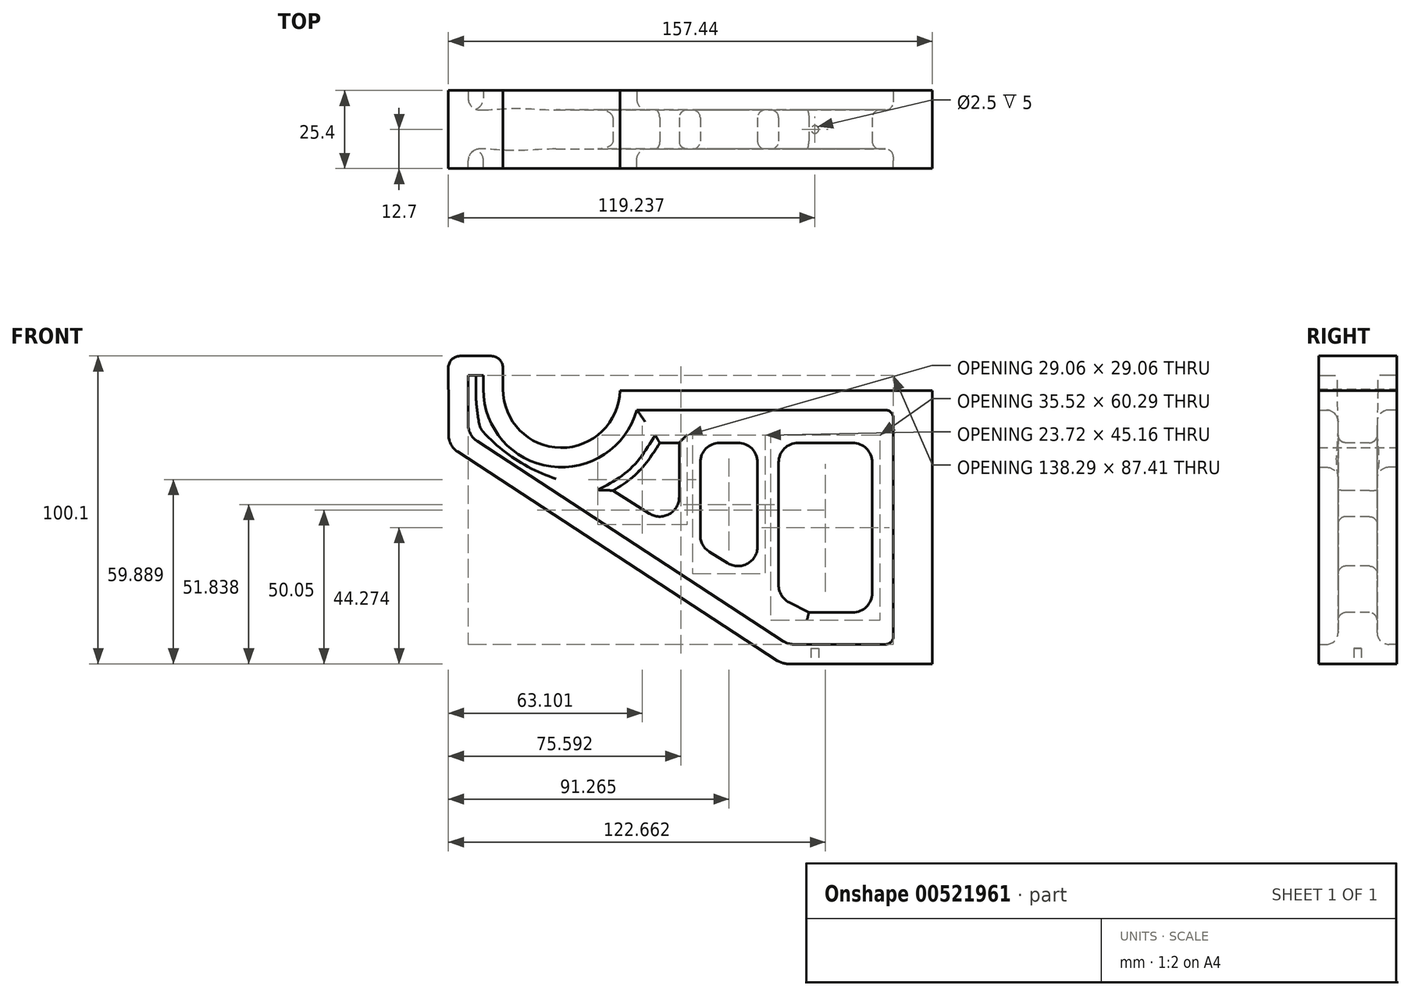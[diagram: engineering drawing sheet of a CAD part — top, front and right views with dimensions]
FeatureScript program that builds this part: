
annotation { "Feature Type Name" : "Feature", "Feature Type Description" : "" }
export const myFeature = defineFeature(function(context is Context, id is Id, definition is map)
    precondition{}
    {
        {
            var Q0;
            Q0=qCreatedBy(makeId("Front.planeOp"),FACE);
            var sketch = newSketch(context, id + "F0", { "sketchPlane" : qUnion([Q0])});
            skLineSegment(sketch, "E0.0", {"start": v(-84.04, 39.62) * mm, "end": v(-84.04, 21.17) * mm});
            skLineSegment(sketch, "E0.1", {"start": v(66.96, 39.19) * mm, "end": v(-28.3, 39.19) * mm});
            skLineSegment(sketch, "E0.2", {"start": v(-84.04, 21.17) * mm, "end": v(24.5, -49.71) * mm});
            skLineSegment(sketch, "E0.3", {"start": v(24.5, -49.71) * mm, "end": v(66.96, -49.71) * mm});
            skLineSegment(sketch, "E0.4", {"start": v(66.96, -49.71) * mm, "end": v(66.96, 39.19) * mm});
            skArc(sketch, "E1", {"start": v(-66.4, 39.62) * mm, "mid": v(-47.56, 20.57) * mm, "end": v(-28.3, 39.19) * mm});
            skLineSegment(sketch, "E2.bottom", {"start": v(-84.04, 39.62) * mm, "end": v(-84.13, 39.62) * mm});
            skLineSegment(sketch, "E2.top", {"start": v(-66.4, 50.4) * mm, "end": v(-84.13, 50.4) * mm});
            skLineSegment(sketch, "E2.left", {"start": v(-66.4, 39.62) * mm, "end": v(-66.4, 50.4) * mm});
            skLineSegment(sketch, "E2.right", {"start": v(-84.13, 39.62) * mm, "end": v(-84.13, 50.4) * mm});
            skLineSegment(sketch, "E3", {"start": v(-47.34, 83.6) * mm, "end": v(-47.34, -33.91) * mm, "construction": true});
            skLineSegment(sketch, "E4", {"start": v(-97.5, 39.62) * mm, "end": v(58.93, 39.62) * mm, "construction": true});
            skLineSegment(sketch, "E5", {"start": v(66.96, -49.71) * mm, "end": v(66.96, 87.18) * mm, "construction": true});
            skSolve(sketch);
        }
        {
            var Q0;
            Q0=makeQuery(id+"F0.imprint","IMPRINT",FACE,{"disambiguationData":[TD([[makeQuery(id+"F0.imprint","IMPRINT",EDGE,{"derivedFrom":sQuery(id+"F0.wireOp",EDGE,"E0.0")}),1.0]])]});
            extrude(context, id + "F1", {"entities" : qUnion([Q0]), "depth" : 6.35 * mm, "offsetDistance" : 25.4 * mm, "hasSecondDirection" : true, "secondDirectionOppositeDirection" : true, "secondDirectionDepth" : 6.35 * mm});
        }
        {
            var Q0;
            Q0=makeQuery(id+"F1.opExtrude","CAP_FACE",FACE,{"disambiguationData":[OSD([sQuery(id+"F0.wireOp",EDGE,"E0.0"),sQuery(id+"F0.wireOp",EDGE,"E0.1"),sQuery(id+"F0.wireOp",EDGE,"E0.2"),sQuery(id+"F0.wireOp",EDGE,"E0.3"),sQuery(id+"F0.wireOp",EDGE,"E0.4"),sQuery(id+"F0.wireOp",EDGE,"E1"),sQuery(id+"F0.wireOp",EDGE,"caf5afc5-a840-4588-9689-efeb098a28d0.trimOffspring")])],"isStart":false});
            shell(context, id + "F2", {"entities" : qUnion([Q0]), "thickness" : 6.35 * mm});
        }
        {
            var Q0;
            Q0=makeQuery(id+"F1.opExtrude","SWEPT_EDGE",EDGE,{"disambiguationData":[OSD([sQuery(id+"F0.wireOp",EDGE,"E0.0"),sQuery(id+"F0.wireOp",EDGE,"E0.2")])]});
            var Q1;
            Q1=makeQuery(id+"F2.opShell","OFFSET_EDGE",EDGE,{"disambiguationData":[OSD([sQuery(id+"F0.wireOp",EDGE,"E0.0"),sQuery(id+"F0.wireOp",EDGE,"E0.2")])]});
            var Q2;
            Q2=makeQuery(id+"F2.opShell","OFFSET_EDGE",EDGE,{"disambiguationData":[OSD([sQuery(id+"F0.wireOp",EDGE,"E0.2"),sQuery(id+"F0.wireOp",EDGE,"E0.3")])]});
            var Q3;
            Q3=makeQuery(id+"F1.opExtrude","SWEPT_EDGE",EDGE,{"disambiguationData":[OSD([sQuery(id+"F0.wireOp",EDGE,"E0.2"),sQuery(id+"F0.wireOp",EDGE,"E0.3")])]});
            var Q4;
            Q4=makeQuery(id+"F1.opExtrude","SWEPT_EDGE",EDGE,{"disambiguationData":[OSD([sQuery(id+"F0.wireOp",EDGE,"E0.0"),sQuery(id+"F0.wireOp",EDGE,"caf5afc5-a840-4588-9689-efeb098a28d0.trimOffspring")])]});
            fillet(context, id + "F3", {"entities" : qUnion([Q0, Q1, Q2, Q3, Q4]), "radius" : 6.35 * mm, "tangentPropagation" : true, "allowEdgeOverflow" : false});
        }
        {
            var Q0;
            Q0=makeQuery(id+"F1.opExtrude","SWEPT_BODY",BODY,{"disambiguationData":[OSD([sQuery(id+"F0.wireOp",EDGE,"E0.0"),sQuery(id+"F0.wireOp",EDGE,"E0.1"),sQuery(id+"F0.wireOp",EDGE,"E0.2"),sQuery(id+"F0.wireOp",EDGE,"E0.3"),sQuery(id+"F0.wireOp",EDGE,"E0.4"),sQuery(id+"F0.wireOp",EDGE,"E1"),sQuery(id+"F0.wireOp",EDGE,"caf5afc5-a840-4588-9689-efeb098a28d0.trimOffspring")])]});
            var Q1;
            Q1=makeQuery(id+"F1.opExtrude","CAP_FACE",FACE,{"disambiguationData":[OSD([sQuery(id+"F0.wireOp",EDGE,"E0.0"),sQuery(id+"F0.wireOp",EDGE,"E0.1"),sQuery(id+"F0.wireOp",EDGE,"E0.2"),sQuery(id+"F0.wireOp",EDGE,"E0.3"),sQuery(id+"F0.wireOp",EDGE,"E0.4"),sQuery(id+"F0.wireOp",EDGE,"E1"),sQuery(id+"F0.wireOp",EDGE,"caf5afc5-a840-4588-9689-efeb098a28d0.trimOffspring")])],"isStart":true});
            mirror(context, id + "F4", {"operationType" : NewBodyOperationType.ADD, "entities" : qUnion([Q0]), "mirrorPlane" : qUnion([Q1])});
        }
        {
            var Q0;
            {var subQ0=makeQuery(id+"F1.opExtrude","SWEPT_EDGE",EDGE,{"disambiguationData":[OSD([sQuery(id+"F0.wireOp",EDGE,"E2.top"),sQuery(id+"F0.wireOp",EDGE,"E2.right")])]});Q0=makeQuery(id+"F4.boolean.opBoolean","MERGE",EDGE,{"derivedFrom":[subQ0,makeQuery(id+"F4.opPattern","COPY",EDGE,{"derivedFrom":subQ0,"instanceName":"1"})]});}
            var Q1;
            {var subQ0=makeQuery(id+"F1.opExtrude","SWEPT_EDGE",EDGE,{"disambiguationData":[OSD([sQuery(id+"F0.wireOp",EDGE,"E2.top"),sQuery(id+"F0.wireOp",EDGE,"E2.left")])]});Q1=makeQuery(id+"F4.boolean.opBoolean","MERGE",EDGE,{"derivedFrom":[subQ0,makeQuery(id+"F4.opPattern","COPY",EDGE,{"derivedFrom":subQ0,"instanceName":"1"})]});}
            var Q2;
            {var subQ0=sQuery(id+"F0.wireOp",EDGE,"E0.2");Q2=makeQuery(id+"F2.opShell","OFFSET_EDGE",EDGE,{"disambiguationData":[OSD([subQ0]),TDD([makeQuery(id+"F1.opExtrude","CAP_EDGE",EDGE,{"disambiguationData":[OSD([subQ0])],"isStart":true})])]});}
            var Q3;
            {var subQ0=sQuery(id+"F0.wireOp",EDGE,"E0.1");Q3=makeQuery(id+"F2.opShell","OFFSET_EDGE",EDGE,{"disambiguationData":[OSD([subQ0]),TDD([makeQuery(id+"F1.opExtrude","CAP_EDGE",EDGE,{"disambiguationData":[OSD([subQ0])],"isStart":true})])]});}
            var Q4;
            {var subQ0=sQuery(id+"F0.wireOp",EDGE,"E1");Q4=makeQuery(id+"F2.opShell","OFFSET_EDGE",EDGE,{"disambiguationData":[OSD([subQ0]),TDD([makeQuery(id+"F1.opExtrude","CAP_EDGE",EDGE,{"disambiguationData":[OSD([subQ0])],"isStart":true})])]});}
            var Q5;
            {var subQ0=sQuery(id+"F0.wireOp",EDGE,"E0.1");Q5=makeQuery(id+"F4.opPattern","COPY",EDGE,{"derivedFrom":makeQuery(id+"F2.opShell","OFFSET_EDGE",EDGE,{"disambiguationData":[OSD([subQ0]),TDD([makeQuery(id+"F1.opExtrude","CAP_EDGE",EDGE,{"disambiguationData":[OSD([subQ0])],"isStart":true})])]}),"instanceName":"1"});}
            var Q6;
            {var subQ0=sQuery(id+"F0.wireOp",EDGE,"E0.2");Q6=makeQuery(id+"F4.opPattern","COPY",EDGE,{"derivedFrom":makeQuery(id+"F2.opShell","OFFSET_EDGE",EDGE,{"disambiguationData":[OSD([subQ0]),TDD([makeQuery(id+"F1.opExtrude","CAP_EDGE",EDGE,{"disambiguationData":[OSD([subQ0])],"isStart":true})])]}),"instanceName":"1"});}
            var Q7;
            {var subQ0=sQuery(id+"F0.wireOp",EDGE,"E1");Q7=makeQuery(id+"F4.opPattern","COPY",EDGE,{"derivedFrom":makeQuery(id+"F2.opShell","OFFSET_EDGE",EDGE,{"disambiguationData":[OSD([subQ0]),TDD([makeQuery(id+"F1.opExtrude","CAP_EDGE",EDGE,{"disambiguationData":[OSD([subQ0])],"isStart":true})])]}),"instanceName":"1"});}
            fillet(context, id + "F5", {"entities" : qUnion([Q0, Q1, Q2, Q3, Q4, Q5, Q6, Q7]), "radius" : 3.8 * mm, "tangentPropagation" : true, "allowEdgeOverflow" : false});
        }
        {
            var Q0;
            Q0=makeQuery(id+"F2.opShell","OFFSET_FACE",FACE,{"disambiguationData":[OSD([sQuery(id+"F0.wireOp",EDGE,"E0.0"),sQuery(id+"F0.wireOp",EDGE,"E0.1"),sQuery(id+"F0.wireOp",EDGE,"E0.2"),sQuery(id+"F0.wireOp",EDGE,"E0.3"),sQuery(id+"F0.wireOp",EDGE,"E0.4"),sQuery(id+"F0.wireOp",EDGE,"E1"),sQuery(id+"F0.wireOp",EDGE,"E2.bottom"),sQuery(id+"F0.wireOp",EDGE,"E2.top"),sQuery(id+"F0.wireOp",EDGE,"E2.left"),sQuery(id+"F0.wireOp",EDGE,"E2.right")])]});
            cPlane(context, id + "F6", {"entities" : qUnion([Q0]), "cplaneType" : CPlaneType.OFFSET, "offset" : 0 * mm, "width" : 152.4 * mm, "height" : 152.4 * mm});
        }
        {
            var Q0;
            Q0=qCreatedBy(id+"F6.planeOp",FACE);
            var sketch = newSketch(context, id + "F7", { "sketchPlane" : qUnion([Q0])});
            skLineSegment(sketch, "E6", {"start": v(29.66, 22.17) * mm, "end": v(47.4, 22.17) * mm});
            skLineSegment(sketch, "E7", {"start": v(53.75, 15.82) * mm, "end": v(53.75, -26.7) * mm});
            skLineSegment(sketch, "E8", {"start": v(47.4, -33.04) * mm, "end": v(33.14, -33.04) * mm});
            skLineSegment(sketch, "E9", {"start": v(33.14, -33.04) * mm, "end": v(26.75, -29.74) * mm});
            skLineSegment(sketch, "E10", {"start": v(23.31, -24.1) * mm, "end": v(23.31, 15.82) * mm});
            skLineSegment(sketch, "E11", {"start": v(10.1, 22.17) * mm, "end": v(4.17, 22.17) * mm});
            skLineSegment(sketch, "E12", {"start": v(-2.18, 15.82) * mm, "end": v(-2.18, -7.91) * mm});
            skLineSegment(sketch, "E13", {"start": v(0.84, -13.32) * mm, "end": v(6.78, -16.97) * mm});
            skLineSegment(sketch, "E14", {"start": v(16.45, -11.56) * mm, "end": v(16.45, 15.82) * mm});
            skLineSegment(sketch, "E15", {"start": v(-15.4, 22.17) * mm, "end": v(-9.04, 22.17) * mm});
            skLineSegment(sketch, "E16", {"start": v(-9.04, 22.17) * mm, "end": v(-9.04, 4.53) * mm});
            skLineSegment(sketch, "E17", {"start": v(-18.8, -0.82) * mm, "end": v(-30.55, 6.66) * mm});
            skFitSpline(sketch, "E18", {"points": [v(-30.55, 6.66) * mm, v(-15.4, 22.17) * mm], "startDerivative": vector(20.62, 11.16) * mm, "endDerivative": vector(13.57, 22.58) * mm});
            skPoint(sketch, "E19.visualSharp", {"position": v(53.75, 22.17) * mm});
            skArc(sketch, "E19.filletArc", {"start": v(53.75, 15.82) * mm, "mid": v(51.9, 20.3) * mm, "end": v(47.4, 22.17) * mm});
            skPoint(sketch, "E20.visualSharp", {"position": v(23.31, 22.17) * mm});
            skArc(sketch, "E20.filletArc", {"start": v(29.66, 22.17) * mm, "mid": v(25.17, 20.3) * mm, "end": v(23.31, 15.82) * mm});
            skPoint(sketch, "E21.visualSharp", {"position": v(53.75, -33.04) * mm});
            skArc(sketch, "E21.filletArc", {"start": v(47.4, -33.04) * mm, "mid": v(51.9, -31.18) * mm, "end": v(53.75, -26.7) * mm});
            skPoint(sketch, "E22.visualSharp", {"position": v(16.45, 22.17) * mm});
            skArc(sketch, "E22.filletArc", {"start": v(16.45, 15.82) * mm, "mid": v(14.6, 20.3) * mm, "end": v(10.1, 22.17) * mm});
            skPoint(sketch, "E23.visualSharp", {"position": v(-2.18, 22.17) * mm});
            skArc(sketch, "E23.filletArc", {"start": v(4.17, 22.17) * mm, "mid": v(-0.32, 20.3) * mm, "end": v(-2.18, 15.82) * mm});
            skPoint(sketch, "E24.visualSharp", {"position": v(-9.04, -7.04) * mm});
            skArc(sketch, "E24.filletArc", {"start": v(-18.8, -0.82) * mm, "mid": v(-12.34, -1.03) * mm, "end": v(-9.04, 4.53) * mm});
            skPoint(sketch, "E25.visualSharp", {"position": v(16.45, -22.93) * mm});
            skArc(sketch, "E25.filletArc", {"start": v(6.78, -16.97) * mm, "mid": v(13.2, -17.1) * mm, "end": v(16.45, -11.56) * mm});
            skPoint(sketch, "E26.visualSharp", {"position": v(23.31, -27.96) * mm});
            skArc(sketch, "E26.filletArc", {"start": v(23.31, -24.1) * mm, "mid": v(24.24, -27.4) * mm, "end": v(26.75, -29.74) * mm});
            skPoint(sketch, "E27.visualSharp", {"position": v(-2.18, -11.46) * mm});
            skArc(sketch, "E27.filletArc", {"start": v(-2.18, -7.91) * mm, "mid": v(-1.38, -11) * mm, "end": v(0.84, -13.32) * mm});
            skSolve(sketch);
        }
        {
            var Q0;
            Q0=makeQuery(id+"F7.imprint","IMPRINT",FACE,{"disambiguationData":[TD([[makeQuery(id+"F7.imprint","IMPRINT",EDGE,{"derivedFrom":sQuery(id+"F7.wireOp",EDGE,"E15")}),-1.0]])]});
            var Q1;
            Q1=makeQuery(id+"F7.imprint","IMPRINT",FACE,{"disambiguationData":[TD([[makeQuery(id+"F7.imprint","IMPRINT",EDGE,{"derivedFrom":sQuery(id+"F7.wireOp",EDGE,"E11")}),1.0]])]});
            var Q2;
            Q2=makeQuery(id+"F7.imprint","IMPRINT",FACE,{"disambiguationData":[TD([[makeQuery(id+"F7.imprint","IMPRINT",EDGE,{"derivedFrom":sQuery(id+"F7.wireOp",EDGE,"E6")}),-1.0]])]});
            extrude(context, id + "F8", {"entities" : qUnion([Q0, Q1, Q2]), "operationType" : NewBodyOperationType.REMOVE, "oppositeDirection" : true, "depth" : 25.4 * mm, "offsetDistance" : 25.4 * mm, "hasSecondDirection" : true, "secondDirectionOppositeDirection" : false, "secondDirectionDepth" : 25.4 * mm});
        }
        {
            var Q0;
            Q0=makeQuery(id+"F8.boolean.opBoolean","INTERSECT",EDGE,{"derivedFrom":[makeQuery(id+"F4.opPattern","COPY",FACE,{"derivedFrom":makeQuery(id+"F2.opShell","OFFSET_FACE",FACE,{"disambiguationData":[OSD([sQuery(id+"F0.wireOp",EDGE,"E0.0"),sQuery(id+"F0.wireOp",EDGE,"E0.1"),sQuery(id+"F0.wireOp",EDGE,"E0.2"),sQuery(id+"F0.wireOp",EDGE,"E0.3"),sQuery(id+"F0.wireOp",EDGE,"E0.4"),sQuery(id+"F0.wireOp",EDGE,"E1"),sQuery(id+"F0.wireOp",EDGE,"E2.bottom"),sQuery(id+"F0.wireOp",EDGE,"E2.top"),sQuery(id+"F0.wireOp",EDGE,"E2.left"),sQuery(id+"F0.wireOp",EDGE,"E2.right")])]}),"instanceName":"1"}),makeQuery(id+"F8.opExtrude","SWEPT_FACE",FACE,{"disambiguationData":[OSD([sQuery(id+"F7.wireOp",EDGE,"E7")])]})]});
            var Q1;
            Q1=makeQuery(id+"F8.boolean.opBoolean","INTERSECT",EDGE,{"derivedFrom":[makeQuery(id+"F2.opShell","OFFSET_FACE",FACE,{"disambiguationData":[OSD([sQuery(id+"F0.wireOp",EDGE,"E0.0"),sQuery(id+"F0.wireOp",EDGE,"E0.1"),sQuery(id+"F0.wireOp",EDGE,"E0.2"),sQuery(id+"F0.wireOp",EDGE,"E0.3"),sQuery(id+"F0.wireOp",EDGE,"E0.4"),sQuery(id+"F0.wireOp",EDGE,"E1"),sQuery(id+"F0.wireOp",EDGE,"E2.bottom"),sQuery(id+"F0.wireOp",EDGE,"E2.top"),sQuery(id+"F0.wireOp",EDGE,"E2.left"),sQuery(id+"F0.wireOp",EDGE,"E2.right")])]}),makeQuery(id+"F8.opExtrude","SWEPT_FACE",FACE,{"disambiguationData":[OSD([sQuery(id+"F7.wireOp",EDGE,"E14")])]})]});
            var Q2;
            Q2=makeQuery(id+"F8.boolean.opBoolean","INTERSECT",EDGE,{"derivedFrom":[makeQuery(id+"F4.opPattern","COPY",FACE,{"derivedFrom":makeQuery(id+"F2.opShell","OFFSET_FACE",FACE,{"disambiguationData":[OSD([sQuery(id+"F0.wireOp",EDGE,"E0.0"),sQuery(id+"F0.wireOp",EDGE,"E0.1"),sQuery(id+"F0.wireOp",EDGE,"E0.2"),sQuery(id+"F0.wireOp",EDGE,"E0.3"),sQuery(id+"F0.wireOp",EDGE,"E0.4"),sQuery(id+"F0.wireOp",EDGE,"E1"),sQuery(id+"F0.wireOp",EDGE,"E2.bottom"),sQuery(id+"F0.wireOp",EDGE,"E2.top"),sQuery(id+"F0.wireOp",EDGE,"E2.left"),sQuery(id+"F0.wireOp",EDGE,"E2.right")])]}),"instanceName":"1"}),makeQuery(id+"F8.opExtrude","SWEPT_FACE",FACE,{"disambiguationData":[OSD([sQuery(id+"F7.wireOp",EDGE,"E16")])]})]});
            var Q3;
            Q3=makeQuery(id+"F4.opPattern","COPY",FACE,{"derivedFrom":makeQuery(id+"F2.opShell","OFFSET_FACE",FACE,{"disambiguationData":[OSD([sQuery(id+"F0.wireOp",EDGE,"E0.0"),sQuery(id+"F0.wireOp",EDGE,"E0.1"),sQuery(id+"F0.wireOp",EDGE,"E0.2"),sQuery(id+"F0.wireOp",EDGE,"E0.3"),sQuery(id+"F0.wireOp",EDGE,"E0.4"),sQuery(id+"F0.wireOp",EDGE,"E1"),sQuery(id+"F0.wireOp",EDGE,"E2.bottom"),sQuery(id+"F0.wireOp",EDGE,"E2.top"),sQuery(id+"F0.wireOp",EDGE,"E2.left"),sQuery(id+"F0.wireOp",EDGE,"E2.right")])]}),"instanceName":"1"});
            var Q4;
            Q4=makeQuery(id+"F8.boolean.opBoolean","INTERSECT",EDGE,{"derivedFrom":[makeQuery(id+"F2.opShell","OFFSET_FACE",FACE,{"disambiguationData":[OSD([sQuery(id+"F0.wireOp",EDGE,"E0.0"),sQuery(id+"F0.wireOp",EDGE,"E0.1"),sQuery(id+"F0.wireOp",EDGE,"E0.2"),sQuery(id+"F0.wireOp",EDGE,"E0.3"),sQuery(id+"F0.wireOp",EDGE,"E0.4"),sQuery(id+"F0.wireOp",EDGE,"E1"),sQuery(id+"F0.wireOp",EDGE,"E2.bottom"),sQuery(id+"F0.wireOp",EDGE,"E2.top"),sQuery(id+"F0.wireOp",EDGE,"E2.left"),sQuery(id+"F0.wireOp",EDGE,"E2.right")])]}),makeQuery(id+"F8.opExtrude","SWEPT_FACE",FACE,{"disambiguationData":[OSD([sQuery(id+"F7.wireOp",EDGE,"E10")])]})]});
            var Q5;
            Q5=makeQuery(id+"F8.boolean.opBoolean","INTERSECT",EDGE,{"derivedFrom":[makeQuery(id+"F2.opShell","OFFSET_FACE",FACE,{"disambiguationData":[OSD([sQuery(id+"F0.wireOp",EDGE,"E0.0"),sQuery(id+"F0.wireOp",EDGE,"E0.1"),sQuery(id+"F0.wireOp",EDGE,"E0.2"),sQuery(id+"F0.wireOp",EDGE,"E0.3"),sQuery(id+"F0.wireOp",EDGE,"E0.4"),sQuery(id+"F0.wireOp",EDGE,"E1"),sQuery(id+"F0.wireOp",EDGE,"E2.bottom"),sQuery(id+"F0.wireOp",EDGE,"E2.top"),sQuery(id+"F0.wireOp",EDGE,"E2.left"),sQuery(id+"F0.wireOp",EDGE,"E2.right")])]}),makeQuery(id+"F8.opExtrude","SWEPT_FACE",FACE,{"disambiguationData":[OSD([sQuery(id+"F7.wireOp",EDGE,"E16")])]})]});
            var Q6;
            Q6=makeQuery(id+"F8.boolean.opBoolean","INTERSECT",EDGE,{"derivedFrom":[makeQuery(id+"F2.opShell","OFFSET_FACE",FACE,{"disambiguationData":[OSD([sQuery(id+"F0.wireOp",EDGE,"E0.0"),sQuery(id+"F0.wireOp",EDGE,"E0.1"),sQuery(id+"F0.wireOp",EDGE,"E0.2"),sQuery(id+"F0.wireOp",EDGE,"E0.3"),sQuery(id+"F0.wireOp",EDGE,"E0.4"),sQuery(id+"F0.wireOp",EDGE,"E1"),sQuery(id+"F0.wireOp",EDGE,"E2.bottom"),sQuery(id+"F0.wireOp",EDGE,"E2.top"),sQuery(id+"F0.wireOp",EDGE,"E2.left"),sQuery(id+"F0.wireOp",EDGE,"E2.right")])]}),makeQuery(id+"F8.opExtrude","SWEPT_FACE",FACE,{"disambiguationData":[OSD([sQuery(id+"F7.wireOp",EDGE,"E18")])]})]});
            var Q7;
            Q7=makeQuery(id+"F8.boolean.opBoolean","INTERSECT",EDGE,{"derivedFrom":[makeQuery(id+"F2.opShell","OFFSET_FACE",FACE,{"disambiguationData":[OSD([sQuery(id+"F0.wireOp",EDGE,"E0.0"),sQuery(id+"F0.wireOp",EDGE,"E0.1"),sQuery(id+"F0.wireOp",EDGE,"E0.2"),sQuery(id+"F0.wireOp",EDGE,"E0.3"),sQuery(id+"F0.wireOp",EDGE,"E0.4"),sQuery(id+"F0.wireOp",EDGE,"E1"),sQuery(id+"F0.wireOp",EDGE,"E2.bottom"),sQuery(id+"F0.wireOp",EDGE,"E2.top"),sQuery(id+"F0.wireOp",EDGE,"E2.left"),sQuery(id+"F0.wireOp",EDGE,"E2.right")])]}),makeQuery(id+"F8.opExtrude","SWEPT_FACE",FACE,{"disambiguationData":[OSD([sQuery(id+"F7.wireOp",EDGE,"E15")])]})]});
            var Q8;
            {var subQ0=sQuery(id+"F0.wireOp",EDGE,"E0.4");Q8=makeQuery(id+"F2.opShell","OFFSET_EDGE",EDGE,{"disambiguationData":[OSD([subQ0]),TDD([makeQuery(id+"F1.opExtrude","CAP_EDGE",EDGE,{"disambiguationData":[OSD([subQ0])],"isStart":true})])]});}
            fillet(context, id + "F9", {"entities" : qUnion([Q0, Q1, Q2, Q3, Q4, Q5, Q6, Q7, Q8]), "radius" : 2.54 * mm, "tangentPropagation" : true, "allowEdgeOverflow" : false});
        }
        {
            var Q0;
            {var subQ0=makeQuery(id+"F1.opExtrude","SWEPT_FACE",FACE,{"disambiguationData":[OSD([sQuery(id+"F0.wireOp",EDGE,"E0.4")])]});Q0=makeQuery(id+"F4.boolean.opBoolean","MERGE",FACE,{"derivedFrom":[subQ0,makeQuery(id+"F4.opPattern","COPY",FACE,{"derivedFrom":subQ0,"instanceName":"1"})]});}
            extrude(context, id + "F10", {"entities" : qUnion([Q0]), "operationType" : NewBodyOperationType.ADD, "depth" : 6.35 * mm, "offsetDistance" : 25.4 * mm});
        }
        {
            var Q0;
            {var subQ0=sQuery(id+"F0.wireOp",EDGE,"E0.3");var subQ1=makeQuery(id+"F1.opExtrude","SWEPT_FACE",FACE,{"disambiguationData":[OSD([subQ0])]});Q0=makeQuery(id+"F10.boolean.opBoolean","MERGE",FACE,{"derivedFrom":[makeQuery(id+"F4.boolean.opBoolean","MERGE",FACE,{"derivedFrom":[subQ1,makeQuery(id+"F4.opPattern","COPY",FACE,{"derivedFrom":subQ1,"instanceName":"1"})]}),makeQuery(id+"F10.opExtrude","SWEPT_FACE",FACE,{"disambiguationData":[OSD([subQ0,sQuery(id+"F0.wireOp",EDGE,"E0.4")])]})]});}
            var sketch = newSketch(context, id + "F11", { "sketchPlane" : qUnion([Q0])});
            skCircle(sketch, "E28", {"center": v(35.1, -6.35) * mm, "radius": 1.25 * mm});
            skPoint(sketch, "E28.centerSnap0", {"position": v(26.39, -6.35) * mm});
            skSolve(sketch);
        }
        {
            var Q0;
            Q0 = qSketchRegion(id + "F11", true);
            extrude(context, id + "F12", {"entities" : qUnion([Q0]), "operationType" : NewBodyOperationType.REMOVE, "oppositeDirection" : true, "depth" : 5 * mm, "offsetDistance" : 25 * mm});
        }
    });
